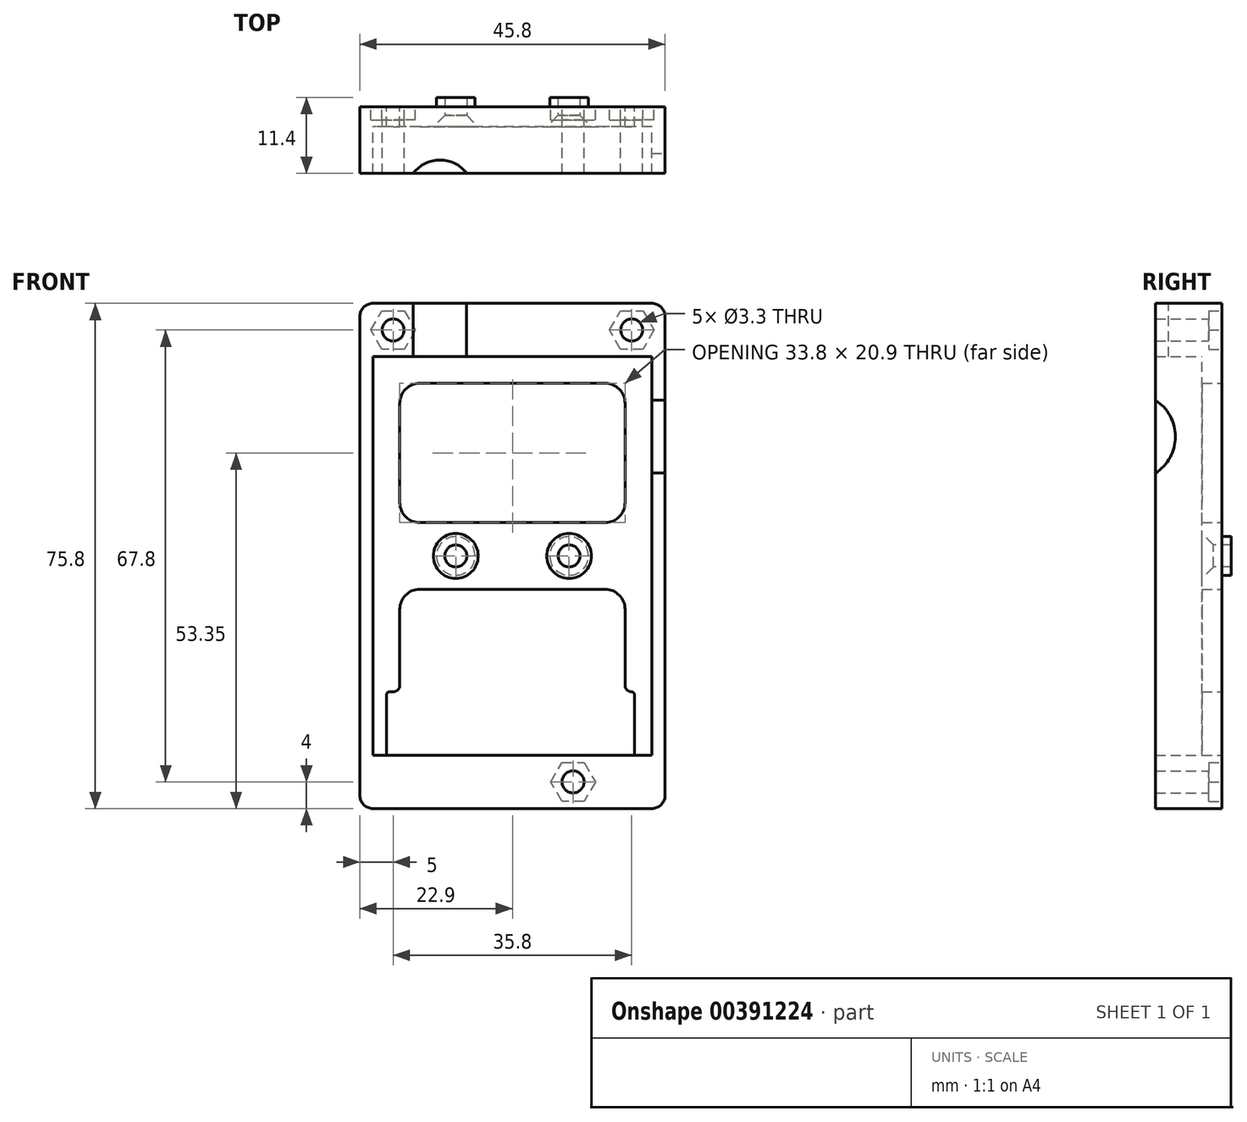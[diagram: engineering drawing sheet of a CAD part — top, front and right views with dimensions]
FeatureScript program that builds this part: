
annotation { "Feature Type Name" : "Feature", "Feature Type Description" : "" }
export const myFeature = defineFeature(function(context is Context, id is Id, definition is map)
    precondition{}
    {
        {
            var Q0;
            Q0=qCreatedBy(makeId("Front.planeOp"),FACE);
            var sketch = newSketch(context, id + "F0", { "sketchPlane" : qUnion([Q0])});
            skLineSegment(sketch, "E0.top", {"start": v(17.9, 37.9) * mm, "end": v(-17.9, 37.9) * mm});
            skPoint(sketch, "E0.middle", {"position": v(0, 0) * mm});
            skLineSegment(sketch, "E1.bottom", {"start": v(20.9, -29.9) * mm, "end": v(-20.9, -29.9) * mm});
            skLineSegment(sketch, "E1.top", {"start": v(20.9, 29.9) * mm, "end": v(-20.9, 29.9) * mm});
            skLineSegment(sketch, "E1.left", {"start": v(20.9, -29.9) * mm, "end": v(20.9, 29.9) * mm});
            skLineSegment(sketch, "E1.right", {"start": v(-20.9, -29.9) * mm, "end": v(-20.9, 29.9) * mm});
            skPoint(sketch, "E2", {"position": v(-16.9, 25.9) * mm});
            skPoint(sketch, "E3", {"position": v(16.9, 25.9) * mm});
            skPoint(sketch, "E4", {"position": v(18.3, -20.39) * mm});
            skPoint(sketch, "E5", {"position": v(-18.88, -20.39) * mm});
            skLineSegment(sketch, "E6", {"start": v(17.9, -20.39) * mm, "end": v(17.9, -20.39) * mm});
            skLineSegment(sketch, "E7", {"start": v(-17.9, -20.39) * mm, "end": v(-18.48, -20.39) * mm});
            skLineSegment(sketch, "E8", {"start": v(-18.88, -20.79) * mm, "end": v(-18.88, -29.9) * mm});
            skLineSegment(sketch, "E9", {"start": v(18.3, -29.9) * mm, "end": v(18.3, -20.79) * mm});
            skPoint(sketch, "E10", {"position": v(-16.9, -20.39) * mm});
            skPoint(sketch, "E11", {"position": v(16.9, -20.39) * mm});
            skLineSegment(sketch, "E12", {"start": v(-13.9, 25.9) * mm, "end": v(13.9, 25.9) * mm});
            skLineSegment(sketch, "E13", {"start": v(-13.9, 5) * mm, "end": v(13.9, 5) * mm});
            skLineSegment(sketch, "E14", {"start": v(-13.9, -5) * mm, "end": v(13.9, -5) * mm});
            skPoint(sketch, "E15", {"position": v(-8.5, 0) * mm});
            skPoint(sketch, "E16", {"position": v(8.5, 0) * mm});
            skCircle(sketch, "E17", {"center": v(-8.5, 0) * mm, "radius": 2.9 * mm});
            skCircle(sketch, "E18", {"center": v(8.5, 0) * mm, "radius": 2.9 * mm});
            skPoint(sketch, "E19.visualSharp", {"position": v(-22.9, 37.9) * mm});
            skPoint(sketch, "E20.visualSharp", {"position": v(22.9, 37.9) * mm});
            skPoint(sketch, "E21.visualSharp", {"position": v(22.9, -37.9) * mm});
            skPoint(sketch, "E22.visualSharp", {"position": v(-22.9, -37.9) * mm});
            skArc(sketch, "E23.filletArc", {"start": v(-13.9, 25.9) * mm, "mid": v(-16.02, 25.02) * mm, "end": v(-16.9, 22.9) * mm});
            skArc(sketch, "E24.filletArc", {"start": v(16.9, 22.9) * mm, "mid": v(16.02, 25.02) * mm, "end": v(13.9, 25.9) * mm});
            skArc(sketch, "E25.filletArc", {"start": v(16.9, -19.39) * mm, "mid": v(17.2, -20.1) * mm, "end": v(17.9, -20.39) * mm});
            skArc(sketch, "E26.filletArc", {"start": v(18.3, -20.79) * mm, "mid": v(18.18, -20.5) * mm, "end": v(17.9, -20.39) * mm});
            skArc(sketch, "E27.filletArc", {"start": v(-17.9, -20.39) * mm, "mid": v(-17.2, -20.1) * mm, "end": v(-16.9, -19.39) * mm});
            skArc(sketch, "E28.filletArc", {"start": v(-18.48, -20.39) * mm, "mid": v(-18.76, -20.5) * mm, "end": v(-18.88, -20.79) * mm});
            skLineSegment(sketch, "E29", {"start": v(-16.9, 22.9) * mm, "end": v(-16.9, 8) * mm});
            skLineSegment(sketch, "E30", {"start": v(16.9, 22.9) * mm, "end": v(16.9, 8) * mm});
            skLineSegment(sketch, "E31", {"start": v(-16.9, -8) * mm, "end": v(-16.9, -19.39) * mm});
            skLineSegment(sketch, "E32", {"start": v(16.9, -8) * mm, "end": v(16.9, -19.39) * mm});
            skPoint(sketch, "E33.visualSharp", {"position": v(-16.9, 5) * mm});
            skArc(sketch, "E33.filletArc", {"start": v(-16.9, 8) * mm, "mid": v(-16.02, 5.88) * mm, "end": v(-13.9, 5) * mm});
            skPoint(sketch, "E34.visualSharp", {"position": v(16.9, 5) * mm});
            skArc(sketch, "E34.filletArc", {"start": v(13.9, 5) * mm, "mid": v(16.02, 5.88) * mm, "end": v(16.9, 8) * mm});
            skPoint(sketch, "E35.visualSharp", {"position": v(16.9, -5) * mm});
            skArc(sketch, "E35.filletArc", {"start": v(16.9, -8) * mm, "mid": v(16.02, -5.88) * mm, "end": v(13.9, -5) * mm});
            skPoint(sketch, "E36.visualSharp", {"position": v(-16.9, -5) * mm});
            skArc(sketch, "E36.filletArc", {"start": v(-13.9, -5) * mm, "mid": v(-16.02, -5.88) * mm, "end": v(-16.9, -8) * mm});
            skLineSegment(sketch, "E37", {"start": v(-22.9, 32.9) * mm, "end": v(-22.9, -35.9) * mm});
            skLineSegment(sketch, "E38", {"start": v(20.9, -37.9) * mm, "end": v(-20.9, -37.9) * mm});
            skLineSegment(sketch, "E39", {"start": v(22.9, -35.9) * mm, "end": v(22.9, 32.9) * mm});
            skPoint(sketch, "E40", {"position": v(-10.9, 37.9) * mm});
            skPoint(sketch, "E41", {"position": v(-17.9, 32.9) * mm});
            skPoint(sketch, "E42", {"position": v(17.9, 32.9) * mm});
            skPoint(sketch, "E43", {"position": v(9.1, -33.9) * mm});
            skPoint(sketch, "E44", {"position": v(-17.9, 33.9) * mm});
            skPoint(sketch, "E45", {"position": v(17.9, 33.9) * mm});
            skCircle(sketch, "E46.cCircle", {"center": v(-17.9, 33.9) * mm, "radius": 2.9 * mm, "construction": true});
            skLineSegment(sketch, "E46.0", {"start": v(-14.55, 33.9) * mm, "end": v(-16.23, 31) * mm});
            skLineSegment(sketch, "E46.1", {"start": v(-16.23, 31) * mm, "end": v(-19.57, 31) * mm});
            skLineSegment(sketch, "E46.2", {"start": v(-19.57, 31) * mm, "end": v(-21.25, 33.9) * mm});
            skLineSegment(sketch, "E46.3", {"start": v(-21.25, 33.9) * mm, "end": v(-19.57, 36.8) * mm});
            skLineSegment(sketch, "E46.4", {"start": v(-19.57, 36.8) * mm, "end": v(-16.23, 36.8) * mm});
            skLineSegment(sketch, "E46.5", {"start": v(-16.23, 36.8) * mm, "end": v(-14.55, 33.9) * mm});
            skPoint(sketch, "E46.0.midPoint", {"position": v(-15.39, 32.45) * mm});
            skCircle(sketch, "E47.cCircle", {"center": v(17.9, 33.9) * mm, "radius": 2.9 * mm, "construction": true});
            skLineSegment(sketch, "E47.0", {"start": v(19.57, 31) * mm, "end": v(16.23, 31) * mm});
            skLineSegment(sketch, "E47.1", {"start": v(16.23, 31) * mm, "end": v(14.55, 33.9) * mm});
            skLineSegment(sketch, "E47.2", {"start": v(14.55, 33.9) * mm, "end": v(16.23, 36.8) * mm});
            skLineSegment(sketch, "E47.3", {"start": v(16.23, 36.8) * mm, "end": v(19.57, 36.8) * mm});
            skLineSegment(sketch, "E47.4", {"start": v(19.57, 36.8) * mm, "end": v(21.25, 33.9) * mm});
            skLineSegment(sketch, "E47.5", {"start": v(21.25, 33.9) * mm, "end": v(19.57, 31) * mm});
            skPoint(sketch, "E47.0.midPoint", {"position": v(17.9, 31) * mm});
            skCircle(sketch, "E48.cCircle", {"center": v(9.1, -33.9) * mm, "radius": 2.9 * mm, "construction": true});
            skLineSegment(sketch, "E48.0", {"start": v(10.77, -31) * mm, "end": v(12.45, -33.9) * mm});
            skLineSegment(sketch, "E48.1", {"start": v(12.45, -33.9) * mm, "end": v(10.77, -36.8) * mm});
            skLineSegment(sketch, "E48.2", {"start": v(10.77, -36.8) * mm, "end": v(7.43, -36.8) * mm});
            skLineSegment(sketch, "E48.3", {"start": v(7.43, -36.8) * mm, "end": v(5.75, -33.9) * mm});
            skLineSegment(sketch, "E48.4", {"start": v(5.75, -33.9) * mm, "end": v(7.43, -31) * mm});
            skLineSegment(sketch, "E48.5", {"start": v(7.43, -31) * mm, "end": v(10.77, -31) * mm});
            skPoint(sketch, "E48.0.midPoint", {"position": v(11.61, -32.45) * mm});
            skLineSegment(sketch, "E49", {"start": v(22.9, 35.9) * mm, "end": v(22.9, 32.9) * mm});
            skLineSegment(sketch, "E50", {"start": v(17.9, 37.9) * mm, "end": v(20.9, 37.9) * mm});
            skLineSegment(sketch, "E51", {"start": v(-17.9, 37.9) * mm, "end": v(-20.9, 37.9) * mm});
            skLineSegment(sketch, "E52", {"start": v(-22.9, 35.9) * mm, "end": v(-22.9, 32.9) * mm});
            skArc(sketch, "E53.filletArc", {"start": v(-20.9, 37.9) * mm, "mid": v(-22.31, 37.31) * mm, "end": v(-22.9, 35.9) * mm});
            skArc(sketch, "E54.filletArc", {"start": v(22.9, 35.9) * mm, "mid": v(22.31, 37.31) * mm, "end": v(20.9, 37.9) * mm});
            skArc(sketch, "E55.filletArc", {"start": v(20.9, -37.9) * mm, "mid": v(22.31, -37.31) * mm, "end": v(22.9, -35.9) * mm});
            skArc(sketch, "E56.filletArc", {"start": v(-22.9, -35.9) * mm, "mid": v(-22.31, -37.31) * mm, "end": v(-20.9, -37.9) * mm});
            skSolve(sketch);
        }
        {
            var Q0;
            Q0=makeQuery(id+"F0.imprint","IMPRINT",FACE,{"disambiguationData":[TD([[makeQuery(id+"F0.imprint","IMPRINT",EDGE,{"derivedFrom":sQuery(id+"F0.wireOp",EDGE,"E0.top")}),1.0]])]});
            var Q1;
            Q1=makeQuery(id+"F0.imprint","IMPRINT",FACE,{"disambiguationData":[TD([[makeQuery(id+"F0.imprint","IMPRINT",EDGE,{"derivedFrom":sQuery(id+"F0.wireOp",EDGE,"E46.0")}),-1.0]])]});
            var Q2;
            Q2=makeQuery(id+"F0.imprint","IMPRINT",FACE,{"disambiguationData":[TD([[makeQuery(id+"F0.imprint","IMPRINT",EDGE,{"derivedFrom":sQuery(id+"F0.wireOp",EDGE,"E47.0")}),-1.0]])]});
            var Q3;
            Q3=makeQuery(id+"F0.imprint","IMPRINT",FACE,{"disambiguationData":[TD([[makeQuery(id+"F0.imprint","IMPRINT",EDGE,{"derivedFrom":sQuery(id+"F0.wireOp",EDGE,"E48.0")}),-1.0]])]});
            extrude(context, id + "F1", {"entities" : qUnion([Q0, Q1, Q2, Q3]), "depth" : 10 * mm});
        }
        {
            var Q0;
            Q0=makeQuery(id+"F0.imprint","IMPRINT",FACE,{"disambiguationData":[TD([[makeQuery(id+"F0.imprint","IMPRINT",EDGE,{"derivedFrom":sQuery(id+"F0.wireOp",EDGE,"E1.top")}),1.0]])]});
            var Q1;
            Q1=makeQuery(id+"F0.imprint","IMPRINT",FACE,{"disambiguationData":[TD([[makeQuery(id+"F0.imprint","IMPRINT",EDGE,{"derivedFrom":sQuery(id+"F0.wireOp",EDGE,"E17")}),1.0]])]});
            var Q2;
            Q2=makeQuery(id+"F0.imprint","IMPRINT",FACE,{"disambiguationData":[TD([[makeQuery(id+"F0.imprint","IMPRINT",EDGE,{"derivedFrom":sQuery(id+"F0.wireOp",EDGE,"E18")}),1.0]])]});
            extrude(context, id + "F2", {"entities" : qUnion([Q0, Q1, Q2]), "operationType" : NewBodyOperationType.ADD, "depth" : 3 * mm});
        }
        {
            var Q0;
            Q0=makeQuery(id+"F1.opExtrude","SWEPT_FACE",FACE,{"disambiguationData":[OSD([sQuery(id+"F0.wireOp",EDGE,"E39")])]});
            var sketch = newSketch(context, id + "F3", { "sketchPlane" : qUnion([Q0])});
            skPoint(sketch, "E57", {"position": v(-5, 17.9) * mm});
            skPoint(sketch, "E58", {"position": v(-13.5, 17.9) * mm});
            skCircle(sketch, "E59", {"center": v(-13.5, 17.9) * mm, "radius": 6.5 * mm});
            skSolve(sketch);
        }
        {
            var Q0;
            Q0=qSketchRegion(id+"F3",true);
            extrude(context, id + "F4", {"entities" : qUnion([Q0]), "operationType" : NewBodyOperationType.REMOVE, "oppositeDirection" : true, "depth" : 4 * mm});
        }
        {
            var Q0;
            Q0=makeQuery(id+"F1.opExtrude","SWEPT_FACE",FACE,{"disambiguationData":[OSD([sQuery(id+"F0.wireOp",EDGE,"E0.top")])]});
            var sketch = newSketch(context, id + "F5", { "sketchPlane" : qUnion([Q0])});
            skPoint(sketch, "E60", {"position": v(-10.87, 0) * mm});
            skPoint(sketch, "E61", {"position": v(-10.87, -13) * mm});
            skCircle(sketch, "E62", {"center": v(-10.87, -13) * mm, "radius": 5 * mm});
            skSolve(sketch);
        }
        {
            var Q0;
            Q0=qSketchRegion(id+"F5",true);
            extrude(context, id + "F6", {"entities" : qUnion([Q0]), "operationType" : NewBodyOperationType.REMOVE, "oppositeDirection" : true, "depth" : 12 * mm});
        }
        {
            var Q0;
            Q0=makeQuery(id+"F0.imprint","IMPRINT",FACE,{"disambiguationData":[TD([[makeQuery(id+"F0.imprint","IMPRINT",EDGE,{"derivedFrom":sQuery(id+"F0.wireOp",EDGE,"E46.0")}),-1.0]])]});
            var Q1;
            Q1=makeQuery(id+"F0.imprint","IMPRINT",FACE,{"disambiguationData":[TD([[makeQuery(id+"F0.imprint","IMPRINT",EDGE,{"derivedFrom":sQuery(id+"F0.wireOp",EDGE,"E47.0")}),-1.0]])]});
            var Q2;
            Q2=makeQuery(id+"F0.imprint","IMPRINT",FACE,{"disambiguationData":[TD([[makeQuery(id+"F0.imprint","IMPRINT",EDGE,{"derivedFrom":sQuery(id+"F0.wireOp",EDGE,"E48.0")}),-1.0]])]});
            extrude(context, id + "F7", {"entities" : qUnion([Q0, Q1, Q2]), "operationType" : NewBodyOperationType.REMOVE, "depth" : 2 * mm});
        }
        {
            var Q0;
            Q0=sQuery(id+"F0.wireOp",VERTEX,"E44");
            var Q1;
            Q1=sQuery(id+"F0.wireOp",VERTEX,"E45");
            var Q2;
            Q2=sQuery(id+"F0.wireOp",VERTEX,"E43");
            var Q3;
            Q3=makeQuery(id+"F1.opExtrude","SWEPT_BODY",BODY,{"disambiguationData":[OSD([sQuery(id+"F0.wireOp",EDGE,"E0.top"),sQuery(id+"F0.wireOp",EDGE,"E1.bottom"),sQuery(id+"F0.wireOp",EDGE,"E1.top"),sQuery(id+"F0.wireOp",EDGE,"E1.left"),sQuery(id+"F0.wireOp",EDGE,"E1.right"),sQuery(id+"F0.wireOp",EDGE,"E19.filletArc"),sQuery(id+"F0.wireOp",EDGE,"E20.filletArc"),sQuery(id+"F0.wireOp",EDGE,"E37"),sQuery(id+"F0.wireOp",EDGE,"E38"),sQuery(id+"F0.wireOp",EDGE,"E39")])]});
            hole(context, id + "F8", {"style" : HoleStyle.SIMPLE, "endStyle" : HoleEndStyle.BLIND, "oppositeDirection" : true, "standardTappedOrClearance" : lookupTablePath({ "standard" : "ISO", "fit" : "Normal", "size" : "M3", "type" : "Clearance" }), "standardBlindInLast" : lookupTablePath({ "fit" : "Standard", "standard" : "ISO", "size" : "M3", "type" : "Clearance" }), "holeDiameter" : 3.3 * mm, "holeDepth" : 13.8 * mm, "tappedDepth" : 12 * mm, "tapClearance" : 3, "locations" : qUnion([Q0, Q1, Q2]), "scope" : qUnion([Q3])});
        }
        {
            var Q0;
            Q0=makeQuery(id+"F0.imprint","IMPRINT",FACE,{"disambiguationData":[TD([[makeQuery(id+"F0.imprint","IMPRINT",EDGE,{"derivedFrom":sQuery(id+"F0.wireOp",EDGE,"E18")}),1.0]])]});
            var Q1;
            Q1=makeQuery(id+"F0.imprint","IMPRINT",FACE,{"disambiguationData":[TD([[makeQuery(id+"F0.imprint","IMPRINT",EDGE,{"derivedFrom":sQuery(id+"F0.wireOp",EDGE,"E17")}),1.0]])]});
            extrude(context, id + "F9", {"entities" : qUnion([Q0, Q1]), "operationType" : NewBodyOperationType.ADD, "oppositeDirection" : true, "depth" : 1.4 * mm});
        }
        {
            var Q0;
            Q0=sQuery(id+"F0.wireOp",VERTEX,"E15");
            var Q1;
            Q1=sQuery(id+"F0.wireOp",VERTEX,"E16");
            var Q2;
            Q2=makeQuery(id+"F1.opExtrude","SWEPT_BODY",BODY,{"disambiguationData":[OSD([sQuery(id+"F0.wireOp",EDGE,"E0.top"),sQuery(id+"F0.wireOp",EDGE,"E1.bottom"),sQuery(id+"F0.wireOp",EDGE,"E1.top"),sQuery(id+"F0.wireOp",EDGE,"E1.left"),sQuery(id+"F0.wireOp",EDGE,"E1.right"),sQuery(id+"F0.wireOp",EDGE,"E37"),sQuery(id+"F0.wireOp",EDGE,"E38"),sQuery(id+"F0.wireOp",EDGE,"E39"),sQuery(id+"F0.wireOp",EDGE,"E49"),sQuery(id+"F0.wireOp",EDGE,"E50"),sQuery(id+"F0.wireOp",EDGE,"E51"),sQuery(id+"F0.wireOp",EDGE,"E52"),sQuery(id+"F0.wireOp",EDGE,"E53.filletArc"),sQuery(id+"F0.wireOp",EDGE,"E54.filletArc"),sQuery(id+"F0.wireOp",EDGE,"E55.filletArc"),sQuery(id+"F0.wireOp",EDGE,"E56.filletArc")])]});
            hole(context, id + "F10", {"style" : HoleStyle.SIMPLE, "endStyle" : HoleEndStyle.BLIND, "standardTappedOrClearance" : lookupTablePath({ "standard" : "ISO", "fit" : "Normal", "size" : "M3", "type" : "Clearance" }), "standardBlindInLast" : lookupTablePath({ "fit" : "Standard", "standard" : "ISO", "size" : "M3", "type" : "Clearance" }), "holeDiameter" : 3.3 * mm, "holeDepth" : 8 * mm, "tappedDepth" : 12 * mm, "tapClearance" : 3, "locations" : qUnion([Q0, Q1]), "scope" : qUnion([Q2])});
        }
        {
            var Q0;
            Q0=makeQuery(id+"F2.opExtrude","CAP_FACE",FACE,{"disambiguationData":[OSD([sQuery(id+"F0.wireOp",EDGE,"E1.bottom"),sQuery(id+"F0.wireOp",EDGE,"E1.top"),sQuery(id+"F0.wireOp",EDGE,"E1.left"),sQuery(id+"F0.wireOp",EDGE,"E1.right"),sQuery(id+"F0.wireOp",EDGE,"E7"),sQuery(id+"F0.wireOp",EDGE,"E8"),sQuery(id+"F0.wireOp",EDGE,"E9"),sQuery(id+"F0.wireOp",EDGE,"E12"),sQuery(id+"F0.wireOp",EDGE,"E13"),sQuery(id+"F0.wireOp",EDGE,"E14"),sQuery(id+"F0.wireOp",EDGE,"E23.filletArc"),sQuery(id+"F0.wireOp",EDGE,"E24.filletArc"),sQuery(id+"F0.wireOp",EDGE,"E25.filletArc"),sQuery(id+"F0.wireOp",EDGE,"E26.filletArc"),sQuery(id+"F0.wireOp",EDGE,"E27.filletArc"),sQuery(id+"F0.wireOp",EDGE,"E28.filletArc"),sQuery(id+"F0.wireOp",EDGE,"E29"),sQuery(id+"F0.wireOp",EDGE,"E30"),sQuery(id+"F0.wireOp",EDGE,"E31"),sQuery(id+"F0.wireOp",EDGE,"E32"),sQuery(id+"F0.wireOp",EDGE,"E33.filletArc"),sQuery(id+"F0.wireOp",EDGE,"E34.filletArc"),sQuery(id+"F0.wireOp",EDGE,"E35.filletArc"),sQuery(id+"F0.wireOp",EDGE,"E36.filletArc")])],"isStart":false});
            var sketch = newSketch(context, id + "F11", { "sketchPlane" : qUnion([Q0])});
            skPoint(sketch, "E63", {"position": v(8.5, 0) * mm});
            skPoint(sketch, "E64", {"position": v(-8.5, 0) * mm});
            skSolve(sketch);
        }
        {
            var Q0;
            Q0=sQuery(id+"F11.wireOp",VERTEX,"E64");
            var Q1;
            Q1=sQuery(id+"F11.wireOp",VERTEX,"E63");
            var Q2;
            Q2=makeQuery(id+"F1.opExtrude","SWEPT_BODY",BODY,{"disambiguationData":[OSD([sQuery(id+"F0.wireOp",EDGE,"E0.top"),sQuery(id+"F0.wireOp",EDGE,"E1.bottom"),sQuery(id+"F0.wireOp",EDGE,"E1.top"),sQuery(id+"F0.wireOp",EDGE,"E1.left"),sQuery(id+"F0.wireOp",EDGE,"E1.right"),sQuery(id+"F0.wireOp",EDGE,"E37"),sQuery(id+"F0.wireOp",EDGE,"E38"),sQuery(id+"F0.wireOp",EDGE,"E39"),sQuery(id+"F0.wireOp",EDGE,"E49"),sQuery(id+"F0.wireOp",EDGE,"E50"),sQuery(id+"F0.wireOp",EDGE,"E51"),sQuery(id+"F0.wireOp",EDGE,"E52"),sQuery(id+"F0.wireOp",EDGE,"E53.filletArc"),sQuery(id+"F0.wireOp",EDGE,"E54.filletArc"),sQuery(id+"F0.wireOp",EDGE,"E55.filletArc"),sQuery(id+"F0.wireOp",EDGE,"E56.filletArc")])]});
            hole(context, id + "F12", {"style" : HoleStyle.C_SINK, "endStyle" : HoleEndStyle.BLIND, "standardTappedOrClearance" : lookupTablePath({ "standard" : "ISO", "fit" : "Normal", "size" : "M3", "type" : "Clearance" }), "standardBlindInLast" : lookupTablePath({ "fit" : "Standard", "standard" : "ISO", "size" : "M3", "type" : "Clearance" }), "holeDiameter" : 3.3 * mm, "cSinkDiameter" : 6.72 * mm, "cSinkAngle" : 90 * degree, "holeDepth" : 8 * mm, "tappedDepth" : 12 * mm, "tapClearance" : 3, "locations" : qUnion([Q0, Q1]), "scope" : qUnion([Q2])});
        }
    });
